annotation { "Feature Type Name" : "Feature", "Feature Type Description" : "" }
export const myFeature = defineFeature(function(context is Context, id is Id, definition is map)
    precondition{}
    {
        {
            var Q0;
            Q0=qCreatedBy(makeId("Top.planeOp"),FACE);
            var sketch = newSketch(context, id + "F0", { "sketchPlane" : qUnion([Q0])});
            skLineSegment(sketch, "E0.bottom", {"start": v(38.1, 25.4) * mm, "end": v(-38.1, 25.4) * mm});
            skLineSegment(sketch, "E0.top", {"start": v(38.1, -25.4) * mm, "end": v(-38.1, -25.4) * mm});
            skLineSegment(sketch, "E0.left", {"start": v(41.91, 21.59) * mm, "end": v(41.91, -21.59) * mm});
            skLineSegment(sketch, "E0.right", {"start": v(-41.91, 21.59) * mm, "end": v(-41.91, -21.59) * mm});
            skPoint(sketch, "E0.middle", {"position": v(0, 0) * mm});
            skPoint(sketch, "E1.visualSharp", {"position": v(-41.91, 25.4) * mm});
            skArc(sketch, "E1.filletArc", {"start": v(-38.1, 25.4) * mm, "mid": v(-40.8, 24.28) * mm, "end": v(-41.91, 21.59) * mm});
            skPoint(sketch, "E2.visualSharp", {"position": v(41.91, -25.4) * mm});
            skArc(sketch, "E2.filletArc", {"start": v(38.1, -25.4) * mm, "mid": v(40.8, -24.28) * mm, "end": v(41.91, -21.59) * mm});
            skPoint(sketch, "E3.visualSharp", {"position": v(41.91, 25.4) * mm});
            skArc(sketch, "E3.filletArc", {"start": v(41.91, 21.59) * mm, "mid": v(40.8, 24.28) * mm, "end": v(38.1, 25.4) * mm});
            skPoint(sketch, "E4.visualSharp", {"position": v(-41.91, -25.4) * mm});
            skArc(sketch, "E4.filletArc", {"start": v(-41.91, -21.59) * mm, "mid": v(-40.8, -24.28) * mm, "end": v(-38.1, -25.4) * mm});
            skCircle(sketch, "E5", {"center": v(-34.6, -18.52) * mm, "radius": 3.18 * mm});
            skSolve(sketch);
        }
        {
            var Q0;
            Q0=makeQuery(id+"F0.imprint","IMPRINT",FACE,{"disambiguationData":[TD([[makeQuery(id+"F0.imprint","IMPRINT",EDGE,{"derivedFrom":sQuery(id+"F0.wireOp",EDGE,"E0.bottom")}),1.0]])]});
            extrude(context, id + "F1", {"entities" : qUnion([Q0]), "depth" : 1.27 * mm, "offsetDistance" : 25.4 * mm});
        }
        {
            var Q0;
            Q0=makeQuery(id+"F1.opExtrude","CAP_FACE",FACE,{"disambiguationData":[OSD([sQuery(id+"F0.wireOp",EDGE,"E0.bottom"),sQuery(id+"F0.wireOp",EDGE,"E0.top"),sQuery(id+"F0.wireOp",EDGE,"E0.left"),sQuery(id+"F0.wireOp",EDGE,"E0.right"),sQuery(id+"F0.wireOp",EDGE,"E1.filletArc"),sQuery(id+"F0.wireOp",EDGE,"E2.filletArc"),sQuery(id+"F0.wireOp",EDGE,"E3.filletArc"),sQuery(id+"F0.wireOp",EDGE,"E4.filletArc"),sQuery(id+"F0.wireOp",EDGE,"E5")])],"isStart":true});
            var sketch = newSketch(context, id + "F2", { "sketchPlane" : qUnion([Q0])});
            skText(sketch, "E6", { "text": "DeltaMaker", "fontName": "OpenSans-Bold.ttf"});
            skText(sketch, "E7", { "text": "Bob Houston\n", "fontName": "OpenSans-BoldItalic.ttf"});
            skText(sketch, "E8", { "text": "407-442-2816", "fontName": "OpenSans-Bold.ttf"});
            const initialGuessF2  = {"E6": [0.03767, -0.01082, -1, 0, 0.00925], "E7": [0.03759, 0.01936, -1, 0, 0.00711], "E8": [0.02317, 0.00298, -1, 0, 0.00573]};
            skSetInitialGuess(sketch, initialGuessF2);
            skSolve(sketch);
        }
        {
            var Q0;
            Q0 = qSketchRegion(id + "F2", true);
            extrude(context, id + "F3", {"entities" : qUnion([Q0]), "operationType" : NewBodyOperationType.REMOVE, "oppositeDirection" : true, "depth" : 0.64 * mm, "offsetDistance" : 25.4 * mm});
        }
    });